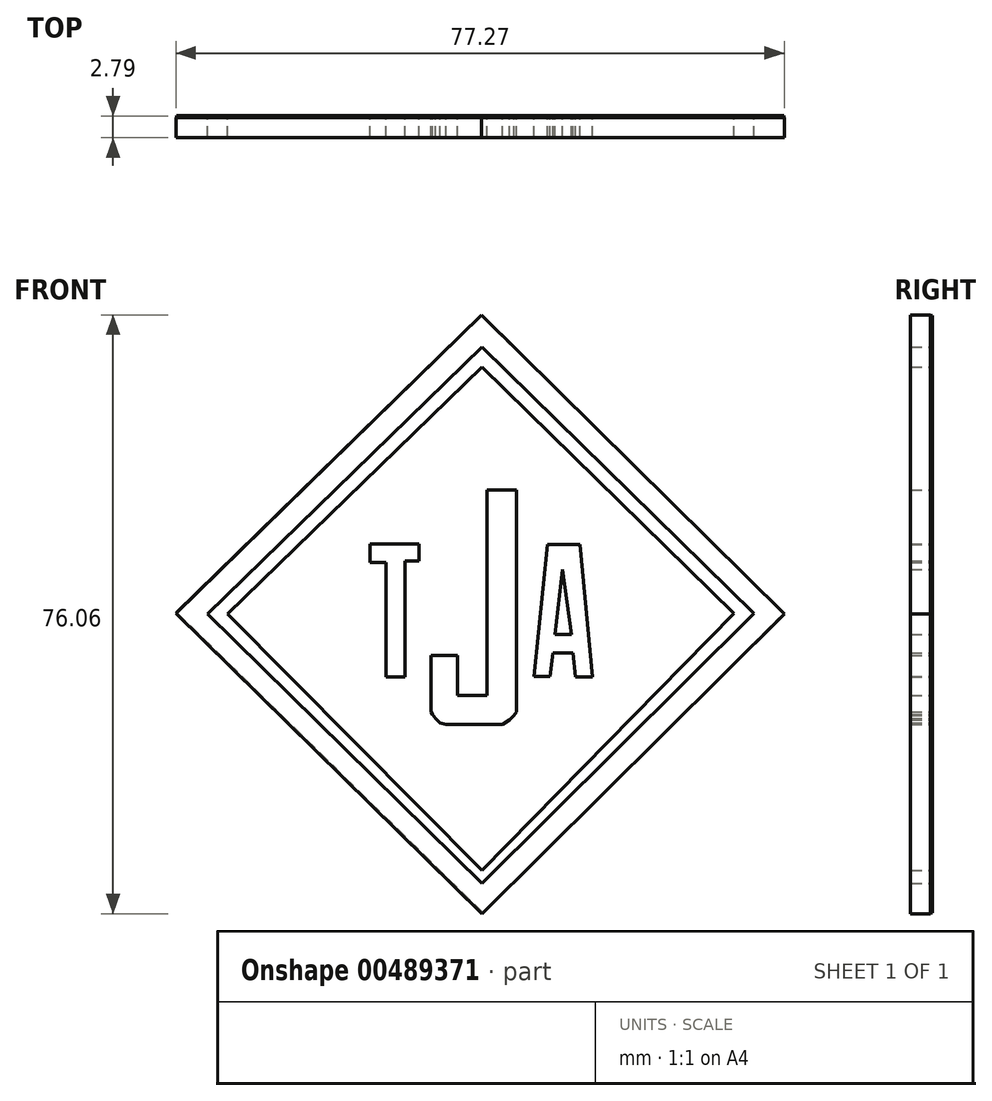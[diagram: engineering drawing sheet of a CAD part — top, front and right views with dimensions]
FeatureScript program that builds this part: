
annotation { "Feature Type Name" : "Feature", "Feature Type Description" : "" }
export const myFeature = defineFeature(function(context is Context, id is Id, definition is map)
    precondition{}
    {
        {
            var Q0;
            Q0=qCreatedBy(makeId("Front.planeOp"),FACE);
            var sketch = newSketch(context, id + "F0", { "sketchPlane" : qUnion([Q0])});
            skLineSegment(sketch, "E0", {"start": v(-37.97, -2.06) * mm, "end": v(0.72, 35.65) * mm});
            skLineSegment(sketch, "E1", {"start": v(0.72, 35.65) * mm, "end": v(39.18, -2.2) * mm});
            skLineSegment(sketch, "E2", {"start": v(39.18, -2.2) * mm, "end": v(0.97, -40.25) * mm});
            skLineSegment(sketch, "E3", {"start": v(0.97, -40.25) * mm, "end": v(-37.97, -2.06) * mm});
            skSolve(sketch);
        }
        {
            var Q0;
            Q0 = qSketchRegion(id + "F0", true);
            extrude(context, id + "F1", {"entities" : qUnion([Q0]), "oppositeDirection" : true, "depth" : 0.25 * mm});
        }
        {
            var Q0;
            Q0=qCreatedBy(makeId("Front.planeOp"),FACE);
            var sketch = newSketch(context, id + "F2", { "sketchPlane" : qUnion([Q0])});
            skLineSegment(sketch, "E4", {"start": v(-38.02, -2.23) * mm, "end": v(0.79, 35.71) * mm});
            skLineSegment(sketch, "E5", {"start": v(0.79, 35.71) * mm, "end": v(39.25, -2.26) * mm});
            skLineSegment(sketch, "E6", {"start": v(39.25, -2.26) * mm, "end": v(0.87, -40.35) * mm});
            skLineSegment(sketch, "E7", {"start": v(0.87, -40.35) * mm, "end": v(-38.02, -2.23) * mm});
            skLineSegment(sketch, "E8", {"start": v(-34.04, -2.26) * mm, "end": v(0.87, -36.49) * mm});
            skLineSegment(sketch, "E9", {"start": v(0.87, -36.49) * mm, "end": v(35.39, -2.23) * mm});
            skLineSegment(sketch, "E10", {"start": v(35.39, -2.23) * mm, "end": v(0.87, 31.6) * mm});
            skLineSegment(sketch, "E11", {"start": v(0.87, 31.6) * mm, "end": v(-34.04, -2.26) * mm});
            skLineSegment(sketch, "E12", {"start": v(-31.47, -2.26) * mm, "end": v(0.87, -34.85) * mm});
            skLineSegment(sketch, "E13", {"start": v(0.87, -34.85) * mm, "end": v(32.85, -2.23) * mm});
            skLineSegment(sketch, "E14", {"start": v(32.85, -2.23) * mm, "end": v(0.87, 29.12) * mm});
            skLineSegment(sketch, "E15", {"start": v(0.87, 29.12) * mm, "end": v(-31.47, -2.26) * mm});
            skLineSegment(sketch, "E16", {"start": v(-13.36, 4.83) * mm, "end": v(-13.36, 6.59) * mm});
            skLineSegment(sketch, "E17", {"start": v(-13.36, 6.59) * mm, "end": v(-7.15, 6.59) * mm});
            skLineSegment(sketch, "E18", {"start": v(-7.15, 6.59) * mm, "end": v(-7.15, 4.43) * mm});
            skLineSegment(sketch, "E19", {"start": v(-7.15, 4.43) * mm, "end": v(-8.9, 4.43) * mm});
            skLineSegment(sketch, "E20", {"start": v(-8.9, 4.43) * mm, "end": v(-8.9, -10.29) * mm});
            skLineSegment(sketch, "E21", {"start": v(-8.9, -10.29) * mm, "end": v(-11.33, -10.29) * mm});
            skLineSegment(sketch, "E22", {"start": v(-11.33, -10.29) * mm, "end": v(-11.33, 4.3) * mm});
            skLineSegment(sketch, "E23", {"start": v(-11.33, 4.3) * mm, "end": v(-13.36, 4.3) * mm});
            skLineSegment(sketch, "E24", {"start": v(-13.36, 4.3) * mm, "end": v(-13.36, 4.83) * mm});
            skLineSegment(sketch, "E25", {"start": v(-5.62, -7.55) * mm, "end": v(-2.24, -7.55) * mm});
            skLineSegment(sketch, "E26", {"start": v(-2.24, -7.55) * mm, "end": v(-2.24, -12.61) * mm});
            skLineSegment(sketch, "E27", {"start": v(-2.24, -12.61) * mm, "end": v(1.45, -12.61) * mm});
            skLineSegment(sketch, "E28", {"start": v(1.45, -12.61) * mm, "end": v(1.45, 13.48) * mm});
            skLineSegment(sketch, "E29", {"start": v(1.45, 13.48) * mm, "end": v(5.23, 13.48) * mm});
            skLineSegment(sketch, "E30", {"start": v(5.23, 13.48) * mm, "end": v(5.23, -14.38) * mm});
            skLineSegment(sketch, "E31", {"start": v(5.23, -14.38) * mm, "end": v(5.23, -14.73) * mm});
            skLineSegment(sketch, "E32", {"start": v(5.23, -14.73) * mm, "end": v(4.94, -15.16) * mm});
            skLineSegment(sketch, "E33", {"start": v(4.94, -15.16) * mm, "end": v(4.36, -15.76) * mm});
            skLineSegment(sketch, "E34", {"start": v(4.36, -15.76) * mm, "end": v(3.46, -16.29) * mm});
            skLineSegment(sketch, "E35", {"start": v(3.46, -16.29) * mm, "end": v(-3.75, -16.29) * mm});
            skLineSegment(sketch, "E36", {"start": v(-3.75, -16.29) * mm, "end": v(-4.47, -16.1) * mm});
            skLineSegment(sketch, "E37", {"start": v(-4.47, -16.1) * mm, "end": v(-5.04, -15.57) * mm});
            skLineSegment(sketch, "E38", {"start": v(-5.04, -15.57) * mm, "end": v(-5.45, -15.02) * mm});
            skLineSegment(sketch, "E39", {"start": v(-5.45, -15.02) * mm, "end": v(-5.62, -14.7) * mm});
            skLineSegment(sketch, "E40", {"start": v(-5.62, -14.7) * mm, "end": v(-5.62, -7.55) * mm});
            skPoint(sketch, "E41.orphan", {"position": v(-5.85, -7.55) * mm});
            skLineSegment(sketch, "E42", {"start": v(7.48, -10.23) * mm, "end": v(9.49, -10.23) * mm});
            skLineSegment(sketch, "E43", {"start": v(9.49, -10.23) * mm, "end": v(9.89, -7.22) * mm});
            skLineSegment(sketch, "E44", {"start": v(9.89, -7.22) * mm, "end": v(12.42, -7.22) * mm});
            skLineSegment(sketch, "E45", {"start": v(12.42, -7.22) * mm, "end": v(12.74, -10.3) * mm});
            skLineSegment(sketch, "E46", {"start": v(12.74, -10.3) * mm, "end": v(14.87, -10.3) * mm});
            skLineSegment(sketch, "E47", {"start": v(14.87, -10.3) * mm, "end": v(13.3, 6.55) * mm});
            skLineSegment(sketch, "E48", {"start": v(13.3, 6.55) * mm, "end": v(9.17, 6.55) * mm});
            skLineSegment(sketch, "E49", {"start": v(9.17, 6.55) * mm, "end": v(7.48, -10.23) * mm});
            skLineSegment(sketch, "E50", {"start": v(10.13, -4.85) * mm, "end": v(11.1, 3.38) * mm});
            skLineSegment(sketch, "E51", {"start": v(11.1, 3.38) * mm, "end": v(12.22, -4.9) * mm});
            skLineSegment(sketch, "E52", {"start": v(12.22, -4.9) * mm, "end": v(10.13, -4.85) * mm});
            skSolve(sketch);
        }
        {
            var Q0;
            Q0 = qSketchRegion(id + "F2", true);
            var Q1;
            Q1=makeQuery(id+"F2.imprint","IMPRINT",FACE,{"disambiguationData":[TD([[makeQuery(id+"F2.imprint","IMPRINT",EDGE,{"derivedFrom":sQuery(id+"F2.wireOp",EDGE,"E12")}),1.0]])]});
            var Q2;
            Q2=makeQuery(id+"F2.imprint","IMPRINT",FACE,{"disambiguationData":[TD([[makeQuery(id+"F2.imprint","IMPRINT",EDGE,{"derivedFrom":sQuery(id+"F2.wireOp",EDGE,"E50")}),-1.0]])]});
            extrude(context, id + "F3", {"entities" : qUnion([Q0, Q1, Q2]), "operationType" : NewBodyOperationType.ADD, "depth" : 2.54 * mm});
        }
    });
